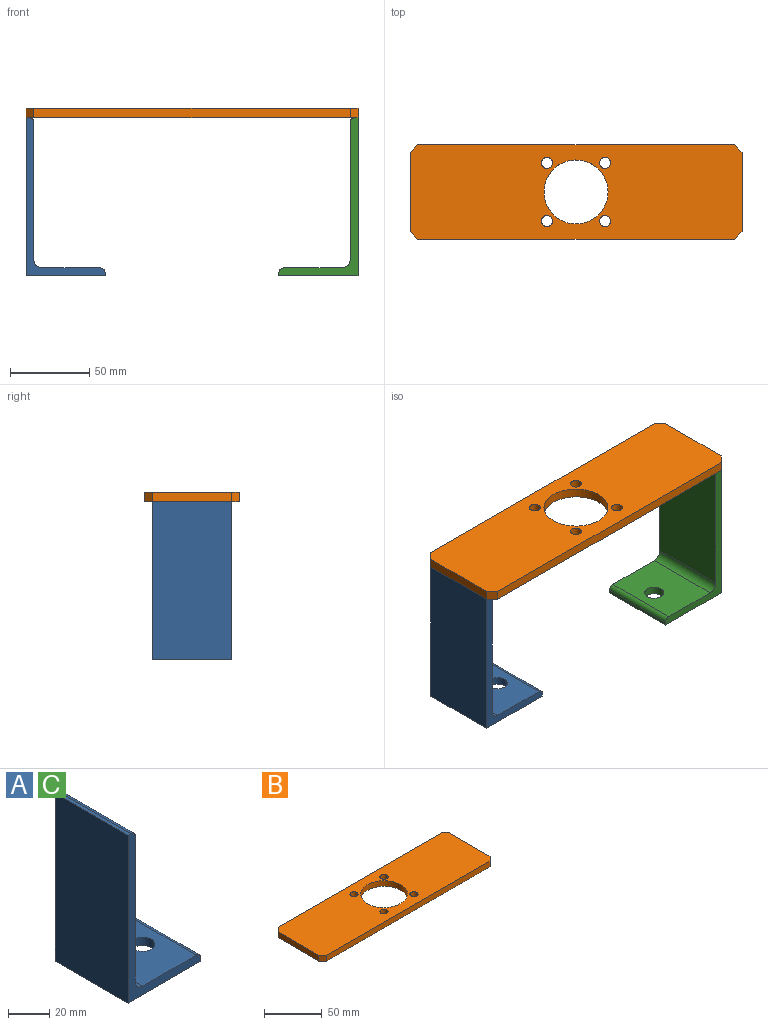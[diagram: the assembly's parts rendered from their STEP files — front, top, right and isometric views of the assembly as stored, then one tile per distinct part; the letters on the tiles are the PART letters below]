
ASSEMBLY  parts=3 mates=4
PART A: 12 faces, bbox 50x50x100 mm
  f0: plane 100x50mm, normal (-1,0,0), area 5000mm2, adj f1,f5,f6,f7
  f1: plane 50x50mm, normal (0,0,-1), area 2386.9mm2, adj f0,f2,f6,f7,f11
  f2: plane 50x2mm, normal (1,0,0), area 100mm2, adj f1,f6,f7,f8
  f3: plane 50x37mm, normal (0,0,1), area 1736.9mm2, adj f6,f7,f8,f10,f11
  f4: plane 87x50mm, normal (1,0,0), area 4350mm2, adj f6,f7,f9,f10
  f5: plane 50x2mm, normal (0,0,1), area 100mm2, adj f0,f6,f7,f9
  f6: plane 100x50mm, normal (0,-1,0), area 726.5mm2, adj f0,f1,f2,f3,f4,f5,f8,f9
  f7: plane 100x50mm, normal (0,1,0), area 726.5mm2, adj f0,f1,f2,f3,f4,f5,f8,f9
  f8: cylinder r=3mm len=50mm, axis (0,1,0), area 235.6mm2, adj f2,f3,f6,f7
  f9: cylinder r=3mm len=50mm, axis (0,1,0), area 235.6mm2, adj f4,f5,f6,f7
  f10: cylinder r=5mm len=50mm, axis (0,-1,0), area 392.7mm2, adj f3,f4,f6,f7
  f11: cylinder r=6mm len=12mm, axis (0,0,-1), area 188.5mm2, adj f1,f3
PART B: 15 faces, bbox 210x60x6 mm
  f0: plane 200x6mm, normal (0,1,0), area 1200mm2, adj f4,f5,f11,f12
  f1: plane 50x6mm, normal (-1,0,0), area 300mm2, adj f4,f5,f11,f14
  f2: plane 200x6mm, normal (0,-1,0), area 1200mm2, adj f4,f5,f13,f14
  f3: plane 50x6mm, normal (1,0,0), area 300mm2, adj f4,f5,f12,f13
  f4: plane 210x60mm, normal (0,0,1), area 11107.8mm2, adj f0,f1,f2,f3,f6,f7,f8,f9
  f5: plane 210x60mm, normal (0,0,-1), area 11107.8mm2, adj f0,f1,f2,f3,f6,f7,f8,f9
  f6: cylinder r=20.25mm len=40.5mm, axis (0,0,-1), area 763.4mm2, adj f4,f5
  f7: cylinder r=3.5mm len=7mm, axis (0,0,-1), area 131.9mm2, adj f4,f5
  f8: cylinder r=3.5mm len=7mm, axis (0,0,-1), area 131.9mm2, adj f4,f5
  f9: cylinder r=3.5mm len=7mm, axis (0,0,-1), area 131.9mm2, adj f4,f5
  f10: cylinder r=3.5mm len=7mm, axis (0,0,-1), area 131.9mm2, adj f4,f5
  f11: plane 6x5mm, normal (-0.71,0.71,0), area 42.4mm2, adj f0,f1,f4,f5
  f12: plane 6x5mm, normal (0.71,0.71,0), area 42.4mm2, adj f0,f3,f4,f5
  f13: plane 6x5mm, normal (0.71,-0.71,0), area 42.4mm2, adj f2,f3,f4,f5
  f14: plane 6x5mm, normal (-0.71,-0.71,0), area 42.4mm2, adj f1,f2,f4,f5
PART C: same geometry as A
PLACE A rot(axis=(0.03,0.06,-1),0deg) t=(-163.33,0,-77.51)mm
PLACE B t=(-58.33,-25,22.49)mm fixed
PLACE C rot(axis=(0,0,-1),180deg) t=(46.67,-50,-77.51)mm
MATE planar A.f1 <-> C.f11  axis (0,0,-1) through (-138.33,-50,-77.51)mm
MATE planar C.f0 <-> B.f3  axis (1,0,0) through (46.67,-50,-27.51)mm
MATE planar C.f5 <-> B.f6  axis (0,0,1) through (45.67,-50,22.49)mm
MATE planar A.f8 <-> C.f8  axis (0,-1,0) through (-116.33,-50,-75.51)mm
